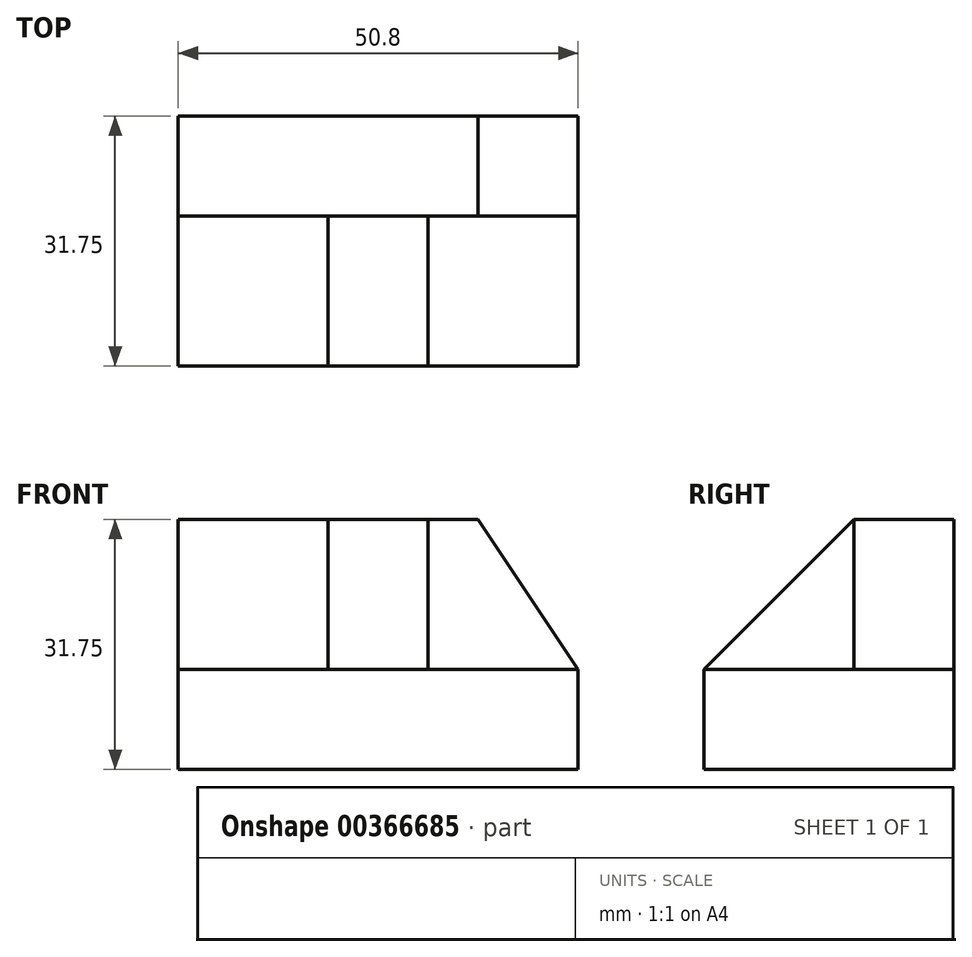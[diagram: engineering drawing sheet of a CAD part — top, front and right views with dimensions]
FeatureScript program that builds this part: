
annotation { "Feature Type Name" : "Feature", "Feature Type Description" : "" }
export const myFeature = defineFeature(function(context is Context, id is Id, definition is map)
    precondition{}
    {
        {
            var Q0;
            Q0=qCreatedBy(makeId("Front.planeOp"),FACE);
            var sketch = newSketch(context, id + "F0", { "sketchPlane" : qUnion([Q0])});
            skLineSegment(sketch, "E0", {"start": v(-57, 0) * mm, "end": v(-57, 31.75) * mm});
            skLineSegment(sketch, "E1", {"start": v(-57, 31.75) * mm, "end": v(-6.2, 31.75) * mm});
            skLineSegment(sketch, "E2", {"start": v(-6.2, 31.75) * mm, "end": v(-6.2, 0) * mm});
            skLineSegment(sketch, "E3", {"start": v(-6.2, 0) * mm, "end": v(-57, 0) * mm});
            skSolve(sketch);
        }
        {
            var Q0;
            Q0=makeQuery(id+"F0.imprint","IMPRINT",FACE,{"disambiguationData":[TD([[makeQuery(id+"F0.imprint","IMPRINT",EDGE,{"derivedFrom":sQuery(id+"F0.wireOp",EDGE,"E0")}),-1.0]])]});
            extrude(context, id + "F1", {"entities" : qUnion([Q0]), "depth" : 31.75 * mm});
        }
        {
            var Q0;
            Q0=makeQuery(id+"F1.opExtrude","CAP_FACE",FACE,{"disambiguationData":[OSD([sQuery(id+"F0.wireOp",EDGE,"E0"),sQuery(id+"F0.wireOp",EDGE,"E1"),sQuery(id+"F0.wireOp",EDGE,"E2"),sQuery(id+"F0.wireOp",EDGE,"E3")])],"isStart":false});
            var sketch = newSketch(context, id + "F2", { "sketchPlane" : qUnion([Q0])});
            skLineSegment(sketch, "E4", {"start": v(-18.9, 31.75) * mm, "end": v(-6.2, 12.7) * mm});
            skSolve(sketch);
        }
        {
            var Q0;
            {var subQ0=sQuery(id+"F2.wireOp",EDGE,"E4");Q0=makeQuery(id+"F2.imprint","IMPRINT",FACE,{"disambiguationData":[TD([[makeQuery(id+"F2.imprint","IMPRINT",EDGE,{"derivedFrom":subQ0}),1.0]])]});}
            extrude(context, id + "F3", {"entities" : qUnion([Q0]), "operationType" : NewBodyOperationType.REMOVE, "oppositeDirection" : true, "depth" : 50.8 * mm});
        }
        {
            var Q0;
            Q0=makeQuery(id+"F1.opExtrude","SWEPT_FACE",FACE,{"disambiguationData":[OSD([sQuery(id+"F0.wireOp",EDGE,"E0")])]});
            var sketch = newSketch(context, id + "F4", { "sketchPlane" : qUnion([Q0])});
            skLineSegment(sketch, "E5", {"start": v(12.7, 31.75) * mm, "end": v(12.7, 12.7) * mm});
            skLineSegment(sketch, "E6", {"start": v(12.7, 12.7) * mm, "end": v(31.75, 12.7) * mm});
            skSolve(sketch);
        }
        {
            var Q0;
            {var subQ0=sQuery(id+"F4.wireOp",EDGE,"E5");Q0=makeQuery(id+"F4.imprint","IMPRINT",FACE,{"disambiguationData":[TD([[makeQuery(id+"F4.imprint","IMPRINT",EDGE,{"derivedFrom":subQ0}),1.0]])]});}
            extrude(context, id + "F5", {"entities" : qUnion([Q0]), "operationType" : NewBodyOperationType.REMOVE, "oppositeDirection" : true, "depth" : 19.05 * mm});
        }
        {
            var Q0;
            Q0=makeQuery(id+"F5.boolean.opBoolean","COPY",FACE,{"derivedFrom":makeQuery(id+"F5.opExtrude","CAP_FACE",FACE,{"disambiguationData":[OSD([sQuery(id+"F0.wireOp",EDGE,"E0"),sQuery(id+"F0.wireOp",EDGE,"E1"),sQuery(id+"F4.wireOp",EDGE,"E5"),sQuery(id+"F4.wireOp",EDGE,"E6")])],"isStart":false})});
            var sketch = newSketch(context, id + "F6", { "sketchPlane" : qUnion([Q0])});
            skLineSegment(sketch, "E7", {"start": v(12.7, 31.75) * mm, "end": v(31.75, 12.7) * mm});
            skSolve(sketch);
        }
        {
            var Q0;
            Q0=makeQuery(id+"F1.opExtrude","CAP_FACE",FACE,{"disambiguationData":[OSD([sQuery(id+"F0.wireOp",EDGE,"E0"),sQuery(id+"F0.wireOp",EDGE,"E1"),sQuery(id+"F0.wireOp",EDGE,"E2"),sQuery(id+"F0.wireOp",EDGE,"E3")])],"isStart":false});
            var sketch = newSketch(context, id + "F7", { "sketchPlane" : qUnion([Q0])});
            skLineSegment(sketch, "E8", {"start": v(-25.26, 31.75) * mm, "end": v(-25.26, 12.7) * mm});
            skLineSegment(sketch, "E9", {"start": v(-25.26, 12.7) * mm, "end": v(-6.2, 12.7) * mm});
            skSolve(sketch);
        }
        {
            var Q0;
            {var subQ0=sQuery(id+"F7.wireOp",EDGE,"E8");Q0=makeQuery(id+"F7.imprint","IMPRINT",FACE,{"disambiguationData":[TD([[makeQuery(id+"F7.imprint","IMPRINT",EDGE,{"derivedFrom":subQ0}),1.0]])]});}
            extrude(context, id + "F8", {"entities" : qUnion([Q0]), "operationType" : NewBodyOperationType.REMOVE, "oppositeDirection" : true, "depth" : 19.05 * mm});
        }
        {
            var Q0;
            Q0=makeQuery(id+"F6.imprint","IMPRINT",FACE,{"disambiguationData":[TD([[makeQuery(id+"F6.imprint","IMPRINT",EDGE,{"derivedFrom":sQuery(id+"F6.wireOp",EDGE,"E7")}),1.0]])]});
            extrude(context, id + "F9", {"entities" : qUnion([Q0]), "operationType" : NewBodyOperationType.REMOVE, "oppositeDirection" : true, "depth" : 25.4 * mm});
        }
    });
